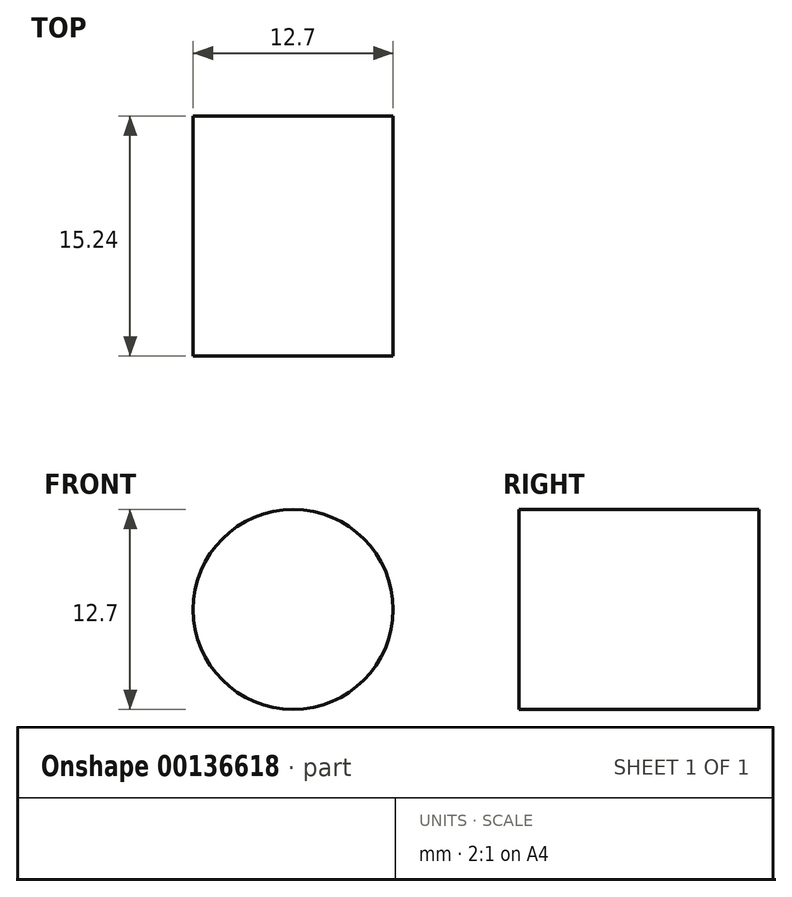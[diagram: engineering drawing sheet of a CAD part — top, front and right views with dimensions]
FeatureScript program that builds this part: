
annotation { "Feature Type Name" : "Feature", "Feature Type Description" : "" }
export const myFeature = defineFeature(function(context is Context, id is Id, definition is map)
    precondition{}
    {
        {
            var Q0;
            Q0=qCreatedBy(makeId("Front.planeOp"),FACE);
            var sketch = newSketch(context, id + "F0", { "sketchPlane" : qUnion([Q0])});
            skCircle(sketch, "E0", {"center": v(0, 0) * mm, "radius": 6.35 * mm});
            skSolve(sketch);
        }
        {
            var Q0;
            Q0 = qSketchRegion(id + "F0", true);
            extrude(context, id + "F1", {"entities" : qUnion([Q0]), "depth" : 15.24 * mm});
        }
    });
